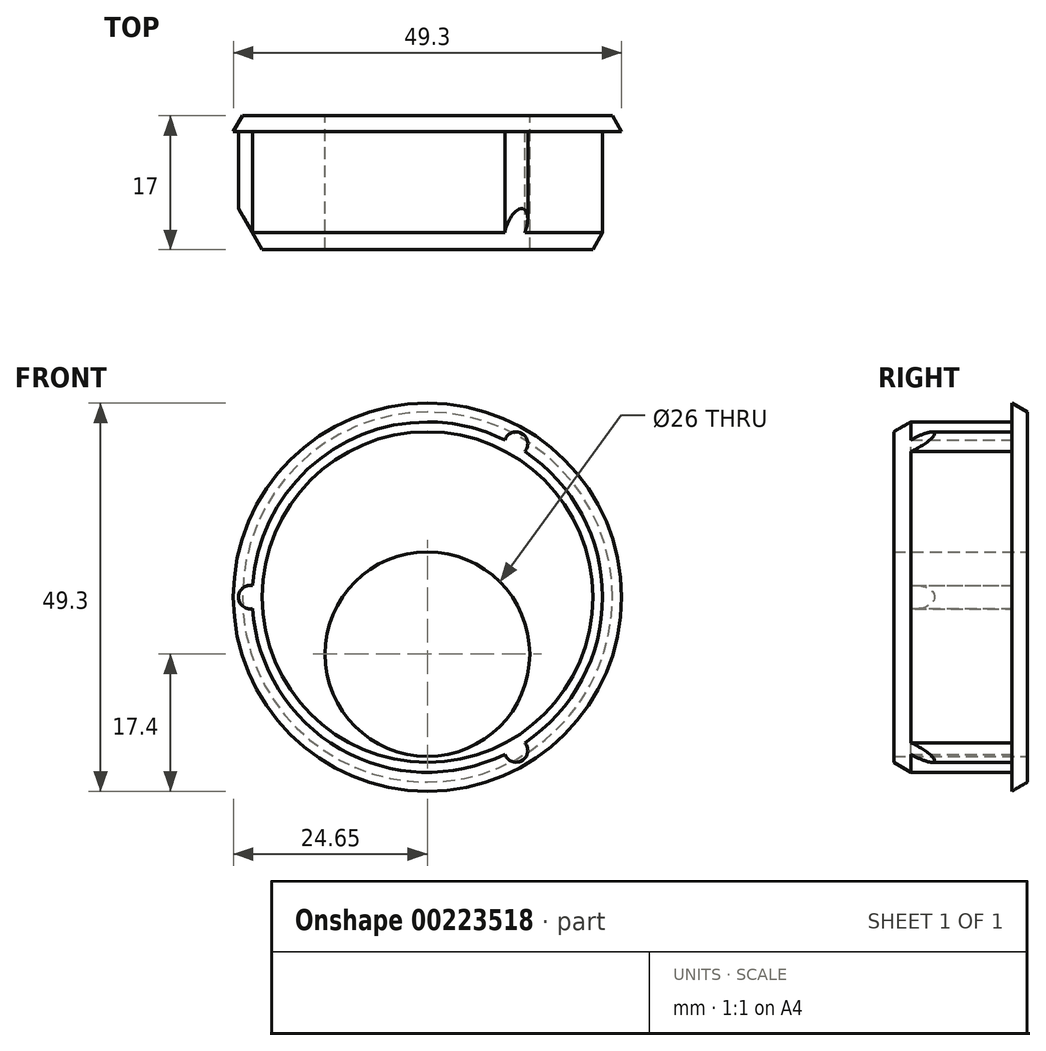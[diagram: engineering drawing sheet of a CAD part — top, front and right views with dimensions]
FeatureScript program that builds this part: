
annotation { "Feature Type Name" : "Feature", "Feature Type Description" : "" }
export const myFeature = defineFeature(function(context is Context, id is Id, definition is map)
    precondition{}
    {
        {
            var Q0;
            Q0=qCreatedBy(makeId("Front.planeOp"),FACE);
            var sketch = newSketch(context, id + "F0", { "sketchPlane" : qUnion([Q0])});
            skCircle(sketch, "E0", {"center": v(0, 0) * mm, "radius": 22.25 * mm});
            skCircle(sketch, "E1", {"center": v(0, -7.25) * mm, "radius": 13 * mm});
            skSolve(sketch);
        }
        {
            var Q0;
            Q0=makeQuery(id+"F0.imprint","IMPRINT",FACE,{"disambiguationData":[TD([[makeQuery(id+"F0.imprint","IMPRINT",EDGE,{"derivedFrom":sQuery(id+"F0.wireOp",EDGE,"E0")}),1.0]])]});
            extrude(context, id + "F1", {"entities" : qUnion([Q0]), "depth" : 15 * mm, "hasSecondDirection" : true, "secondDirectionOppositeDirection" : true, "secondDirectionDepth" : 2 * mm});
        }
        {
            var Q0;
            Q0=qCreatedBy(makeId("Top.planeOp"),FACE);
            var sketch = newSketch(context, id + "F2", { "sketchPlane" : qUnion([Q0])});
            skLineSegment(sketch, "E2", {"start": v(-21.5, 0) * mm, "end": v(-21.5, 2) * mm});
            skLineSegment(sketch, "E3", {"start": v(-21.5, 2) * mm, "end": v(-23.5, 2) * mm});
            skLineSegment(sketch, "E4", {"start": v(-23.5, 2) * mm, "end": v(-24.65, 0) * mm});
            skLineSegment(sketch, "E5", {"start": v(-24.65, 0) * mm, "end": v(-21.5, 0) * mm});
            skCircle(sketch, "E6", {"center": v(-21.75, -11.22) * mm, "radius": 1 * mm});
            skCircle(sketch, "E7", {"center": v(-21.75, -4.12) * mm, "radius": 1 * mm});
            skLineSegment(sketch, "E8", {"start": v(-22.75, -11.22) * mm, "end": v(-22.75, -4.12) * mm, "construction": true});
            skSolve(sketch);
        }
        {
            var Q0;
            Q0=makeQuery(id+"F2.imprint","IMPRINT",FACE,{"disambiguationData":[TD([[makeQuery(id+"F2.imprint","IMPRINT",EDGE,{"derivedFrom":sQuery(id+"F2.wireOp",EDGE,"E2")}),1.0]])]});
            var Q1;
            Q1=makeQuery(id+"F1.opExtrude","SWEPT_FACE",FACE,{"disambiguationData":[OSD([sQuery(id+"F0.wireOp",EDGE,"E0")])]});
            revolve(context, id + "F3", {"operationType" : NewBodyOperationType.ADD, "entities" : qUnion([Q0]), "axis" : qUnion([Q1]), "revolveType" : RevolveType.FULL});
        }
        {
            var Q0;
            Q0=qCreatedBy(makeId("Front.planeOp"),FACE);
            var sketch = newSketch(context, id + "F4", { "sketchPlane" : qUnion([Q0])});
            skCircle(sketch, "E9", {"center": v(0, 0) * mm, "radius": 24 * mm, "construction": true});
            skCircle(sketch, "E10", {"center": v(-22.5, 0) * mm, "radius": 1.5 * mm});
            skCircle(sketch, "E11.1.0", {"center": v(11.25, -19.49) * mm, "radius": 1.5 * mm});
            skCircle(sketch, "E11.2.0", {"center": v(11.25, 19.49) * mm, "radius": 1.5 * mm});
            skSolve(sketch);
        }
        {
            var Q0;
            Q0 = qSketchRegion(id + "F4", true);
            var Q1;
            Q1=makeQuery(id+"F1.opExtrude","CAP_FACE",FACE,{"disambiguationData":[OSD([sQuery(id+"F0.wireOp",EDGE,"E0"),sQuery(id+"F0.wireOp",EDGE,"E1")])],"isStart":false});
            extrude(context, id + "F5", {"entities" : qUnion([Q0]), "operationType" : NewBodyOperationType.ADD, "endBound" : BoundingType.UP_TO_SURFACE, "endBoundEntityFace" : qUnion([Q1]), "depth" : 25 * mm});
        }
        {
            var Q0;
            Q0=qCreatedBy(makeId("Top.planeOp"),FACE);
            var sketch = newSketch(context, id + "F6", { "sketchPlane" : qUnion([Q0])});
            skLineSegment(sketch, "E12", {"start": v(-21, -15) * mm, "end": v(-24.81, -15) * mm});
            skLineSegment(sketch, "E13", {"start": v(-24.81, -15) * mm, "end": v(-24.81, -8.4) * mm});
            skLineSegment(sketch, "E14", {"start": v(-24.81, -8.4) * mm, "end": v(-21, -15) * mm});
            skSolve(sketch);
        }
        {
            var Q0;
            Q0 = qSketchRegion(id + "F6", true);
            var Q1;
            {var subQ0=sQuery(id+"F4.wireOp",EDGE,"E11.2.0");var subQ1=sQuery(id+"F4.wireOp",EDGE,"E10");var subQ2=sQuery(id+"F0.wireOp",EDGE,"E1");var subQ3=sQuery(id+"F0.wireOp",EDGE,"E0");Q1=makeQuery(id+"F5.boolean.opBoolean","SPLIT",FACE,{"disambiguationData":[TD([makeQuery(id+"F1.opExtrude","CAP_FACE",FACE,{"disambiguationData":[OSD([subQ3,subQ2])],"isStart":false}),makeQuery(id+"F3.opRevolve","SWEPT_FACE",FACE,{"disambiguationData":[OSD([sQuery(id+"F2.wireOp",EDGE,"E5")])]}),makeQuery(id+"F5.opExtrude","SWEPT_FACE",FACE,{"disambiguationData":[OSD([subQ1])]}),makeQuery(id+"F5.opExtrude","SWEPT_FACE",FACE,{"disambiguationData":[OSD([subQ0])]}),makeQuery(id+"F5.opExtrude","CAP_FACE",FACE,{"disambiguationData":[OSD([subQ3,subQ2]),ownerDisambiguation([makeQuery(id+"F5.opExtrude","SWEPT_BODY",BODY,{"disambiguationData":[OSD([subQ1])]})])],"isStart":false}),makeQuery(id+"F5.opExtrude","CAP_FACE",FACE,{"disambiguationData":[OSD([subQ3,subQ2]),ownerDisambiguation([makeQuery(id+"F5.opExtrude","SWEPT_BODY",BODY,{"disambiguationData":[OSD([sQuery(id+"F4.wireOp",EDGE,"E11.1.0")])]})])],"isStart":false}),makeQuery(id+"F5.opExtrude","CAP_FACE",FACE,{"disambiguationData":[OSD([subQ3,subQ2]),ownerDisambiguation([makeQuery(id+"F5.opExtrude","SWEPT_BODY",BODY,{"disambiguationData":[OSD([subQ0])]})])],"isStart":false})])],"derivedFrom":makeQuery(id+"F1.opExtrude","SWEPT_FACE",FACE,{"disambiguationData":[OSD([subQ3])]})});}
            revolve(context, id + "F7", {"operationType" : NewBodyOperationType.REMOVE, "entities" : qUnion([Q0]), "axis" : qUnion([Q1]), "revolveType" : RevolveType.FULL, "oppositeDirection" : true});
        }
    });
